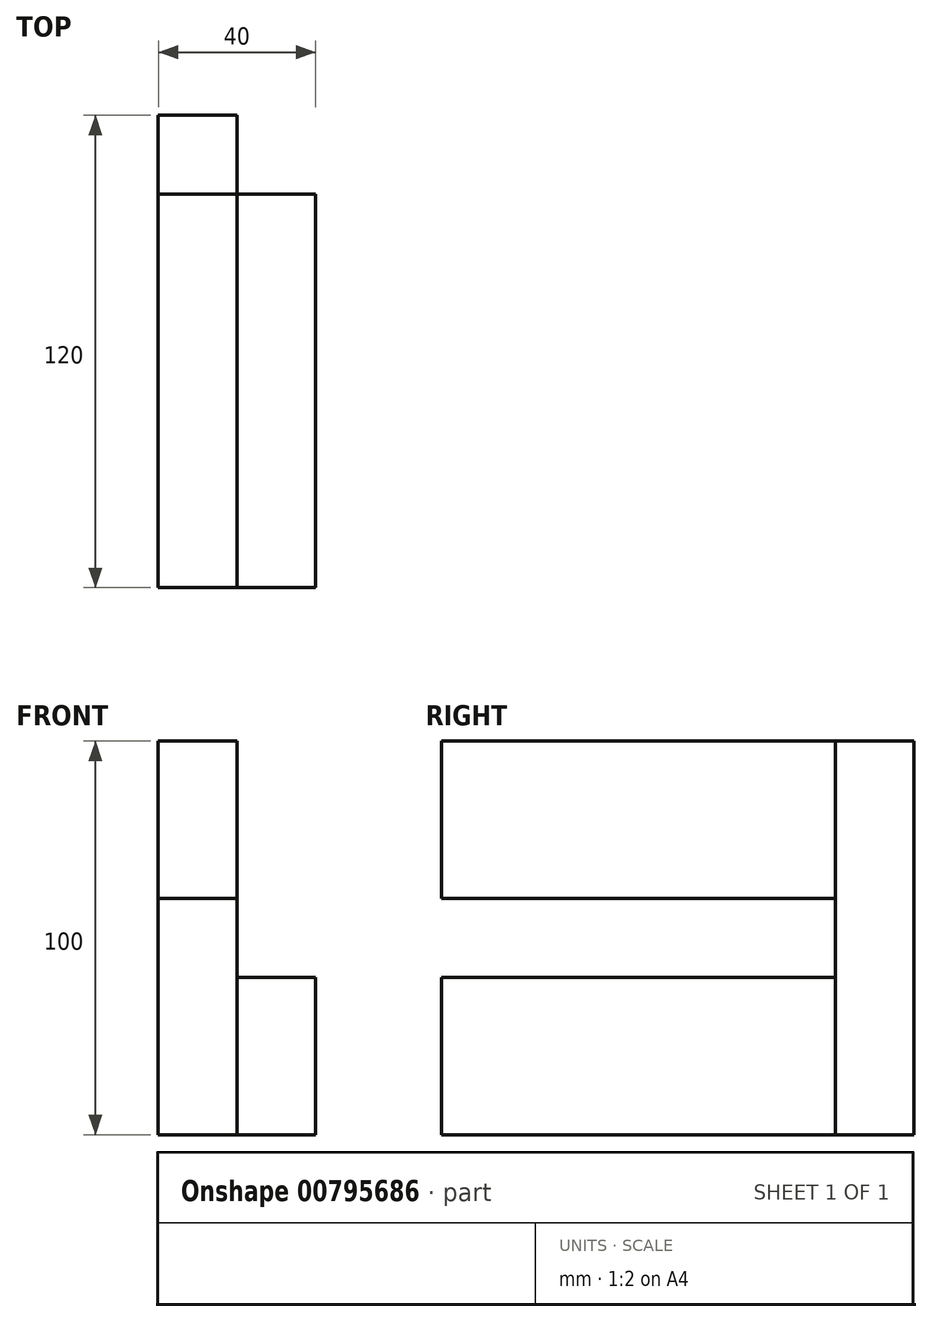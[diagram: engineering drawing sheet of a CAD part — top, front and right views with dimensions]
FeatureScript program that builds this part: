
annotation { "Feature Type Name" : "Feature", "Feature Type Description" : "" }
export const myFeature = defineFeature(function(context is Context, id is Id, definition is map)
    precondition{}
    {
        {
            var Q0;
            Q0=qCreatedBy(makeId("Front.planeOp"),FACE);
            var sketch = newSketch(context, id + "F0", { "sketchPlane" : qUnion([Q0])});
            skLineSegment(sketch, "E0.bottom", {"start": v(-31.82, 24.2) * mm, "end": v(-11.82, 24.2) * mm});
            skLineSegment(sketch, "E0.top", {"start": v(-31.82, -15.8) * mm, "end": v(-11.82, -15.8) * mm});
            skLineSegment(sketch, "E0.left", {"start": v(-31.82, 24.2) * mm, "end": v(-31.82, -15.8) * mm});
            skLineSegment(sketch, "E0.right", {"start": v(-11.82, 24.2) * mm, "end": v(-11.82, -15.8) * mm});
            skSolve(sketch);
        }
        {
            var Q0;
            Q0 = qSketchRegion(id + "F0", true);
            extrude(context, id + "F1", {"entities" : qUnion([Q0]), "depth" : 100 * mm, "offsetDistance" : 25 * mm});
        }
        {
            var Q0;
            Q0=makeQuery(id+"F1.opExtrude","SWEPT_FACE",FACE,{"disambiguationData":[OSD([sQuery(id+"F0.wireOp",EDGE,"E0.right")])]});
            var sketch = newSketch(context, id + "F2", { "sketchPlane" : qUnion([Q0])});
            skLineSegment(sketch, "E1.bottom", {"start": v(0, 24.2) * mm, "end": v(20, 24.2) * mm});
            skLineSegment(sketch, "E1.top", {"start": v(0, -75.8) * mm, "end": v(20, -75.8) * mm});
            skLineSegment(sketch, "E1.left", {"start": v(0, 24.2) * mm, "end": v(0, -75.8) * mm});
            skLineSegment(sketch, "E1.right", {"start": v(20, 24.2) * mm, "end": v(20, -75.8) * mm});
            skSolve(sketch);
        }
        {
            var Q0;
            Q0 = qSketchRegion(id + "F2", true);
            extrude(context, id + "F3", {"entities" : qUnion([Q0]), "oppositeDirection" : true, "depth" : 20 * mm, "offsetDistance" : 25 * mm});
        }
        {
            var Q0;
            Q0=makeQuery(id+"F3.opExtrude","CAP_FACE",FACE,{"disambiguationData":[OSD([sQuery(id+"F2.wireOp",EDGE,"E1.bottom"),sQuery(id+"F2.wireOp",EDGE,"E1.top"),sQuery(id+"F2.wireOp",EDGE,"E1.left"),sQuery(id+"F2.wireOp",EDGE,"E1.right")])],"isStart":true});
            var sketch = newSketch(context, id + "F4", { "sketchPlane" : qUnion([Q0])});
            skLineSegment(sketch, "E2.bottom", {"start": v(0, -75.8) * mm, "end": v(-100, -75.8) * mm});
            skLineSegment(sketch, "E2.top", {"start": v(0, -35.8) * mm, "end": v(-100, -35.8) * mm});
            skLineSegment(sketch, "E2.left", {"start": v(0, -75.8) * mm, "end": v(0, -35.8) * mm});
            skLineSegment(sketch, "E2.right", {"start": v(-100, -75.8) * mm, "end": v(-100, -35.8) * mm});
            skSolve(sketch);
        }
        {
            var Q0;
            Q0 = qSketchRegion(id + "F4", true);
            extrude(context, id + "F5", {"entities" : qUnion([Q0]), "depth" : 20 * mm, "offsetDistance" : 25 * mm});
        }
    });
